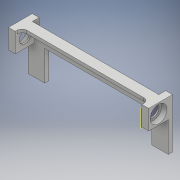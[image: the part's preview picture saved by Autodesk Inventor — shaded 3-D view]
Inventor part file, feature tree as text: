
AUTODESK INVENTOR PART (.ipt)
format: ipt  version: 2018 (Build 220112000, 112)  size: 233,472 bytes
history: native  units: mm
features: sketch x13, extrude x10, plane x1, fillet x1
ambient origin geometry x8: Origin, YZ Plane, XZ Plane, XY Plane, X Axis, Y Axis, Z Axis, Center Point
bodies: Solid1 (feature_tree)
feature tree (25):
  extrude  "Extrusion1"  Depth=22.5mm
  extrude  "Extrusion2"  Depth=26.0mm
  extrude  "Extrusion3"  Depth=9.0mm TaperAngle=0.0deg
  extrude  "Extrusion4"  Depth=2.0mm TaperAngle=0.0deg
  extrude  "Extrusion5"  Depth=26.0mm
  extrude  "Extrusion6"  Depth=9.0mm TaperAngle=0.0deg
  plane  "Work Plane1"
  extrude  "Extrusion7"  Depth=5.5mm TaperAngle=0.0deg
  sketch  "Sketch8"  dims[d20=0.0mm d21=9.25mm d22=9.0mm]
  sketch  "Sketch9"  dims[d23=168.0mm d24=0.0mm d25=9.0mm]
  extrude  "Extrusion8"  Depth=9.25mm
  fillet  "Fillet1"  Radius=9.0mm
  sketch  "Sketch11"  dims[d29=22.0mm]
  extrude  "Extrusion9"  Depth=9.0mm
  extrude  "Extrusion10"  Depth=6.5mm
  sketch  "Sketch1"  dims[d0=22.5mm d1=3.0mm]
  sketch  "Sketch2"  dims[d2=3.0mm d3=26.0mm]
  sketch  "Sketch3"  dims[d4=26.0mm d5=9.0mm d6=0.0mm]
  sketch  "Sketch4"  dims[d7=15.5mm d8=2.0mm d9=0.0mm]
  sketch  "Sketch5"  dims[d10=4.25mm d11=26.0mm]
  sketch  "Sketch6"  dims[d12=168.0mm d13=0.0mm d14=9.0mm d15=0.0mm]
  sketch  "Sketch7"  dims[d16=2.0mm d17=0.0mm d18=5.5mm d19=0.0mm]
  sketch  "Sketch10"  dims[d26=5.0mm d27=0.0mm d28=6.5mm]
  sketch  "Sketch12"  dims[d30=12.2mm]
  sketch  "Sketch13"  dims[d31=3.2mm d32=22.0mm d33=12.2mm d34=3.2mm d35=40.0mm d36=0.0mm d37=15.0mm d38=0.0mm]
